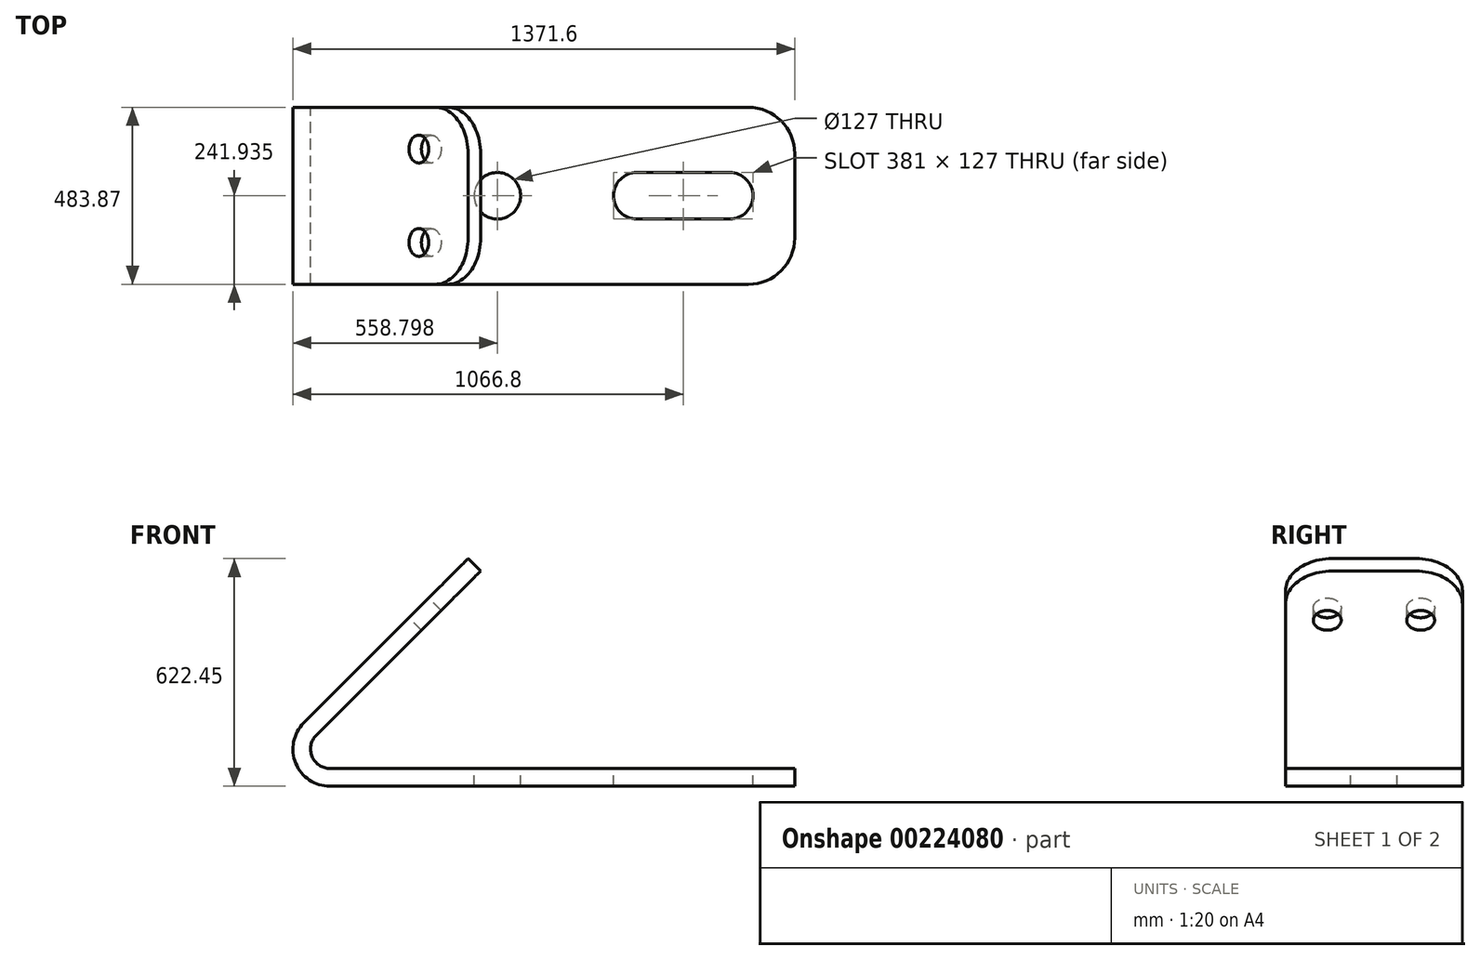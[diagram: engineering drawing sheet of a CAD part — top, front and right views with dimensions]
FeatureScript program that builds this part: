
annotation { "Feature Type Name" : "Feature", "Feature Type Description" : "" }
export const myFeature = defineFeature(function(context is Context, id is Id, definition is map)
    precondition{}
    {
        {
            var Q0;
            Q0=qCreatedBy(makeId("Front.planeOp"),FACE);
            var sketch = newSketch(context, id + "F0", { "sketchPlane" : qUnion([Q0])});
            skLineSegment(sketch, "E0", {"start": v(713.7, 0) * mm, "end": v(-556.3, 0) * mm});
            skLineSegment(sketch, "E1", {"start": v(-628.14, 173.44) * mm, "end": v(-179.13, 622.45) * mm});
            skPoint(sketch, "E2.visualSharp", {"position": v(-801.59, 0) * mm});
            skArc(sketch, "E2.filletArc", {"start": v(-628.14, 173.44) * mm, "mid": v(-650.17, 62.72) * mm, "end": v(-556.3, 0) * mm});
            skLineSegment(sketch, "E3", {"start": v(713.7, 0) * mm, "end": v(713.7, 48.26) * mm});
            skLineSegment(sketch, "E4", {"start": v(713.7, 48.26) * mm, "end": v(-556.3, 48.26) * mm});
            skLineSegment(sketch, "E5", {"start": v(-179.13, 622.45) * mm, "end": v(-145, 588.33) * mm});
            skLineSegment(sketch, "E6", {"start": v(-145, 588.33) * mm, "end": v(-594.02, 139.32) * mm});
            skPoint(sketch, "E7.newPointB", {"position": v(0, 48.26) * mm});
            skArc(sketch, "E7.filletArc", {"start": v(-594.02, 139.32) * mm, "mid": v(-605.58, 81.19) * mm, "end": v(-556.3, 48.26) * mm});
            skSolve(sketch);
        }
        {
            var Q0;
            Q0 = qSketchRegion(id + "F0", true);
            extrude(context, id + "F1", {"entities" : qUnion([Q0]), "depth" : 483.87 * mm});
        }
        {
            var Q0;
            Q0=makeQuery(id+"F1.opExtrude","SWEPT_FACE",FACE,{"disambiguationData":[OSD([sQuery(id+"F0.wireOp",EDGE,"E1")])]});
            var sketch = newSketch(context, id + "F2", { "sketchPlane" : qUnion([Q0])});
            skLineSegment(sketch, "E8", {"start": v(241.94, 313.48) * mm, "end": v(241.94, -745.94) * mm, "construction": true});
            skPoint(sketch, "E8.endSnap0", {"position": v(241.94, -321.52) * mm});
            skCircle(sketch, "E9", {"center": v(114.3, 122.98) * mm, "radius": 38.1 * mm});
            skCircle(sketch, "E10.MirrorC", {"center": v(369.57, 122.98) * mm, "radius": 38.1 * mm});
            skSolve(sketch);
        }
        {
            var Q0;
            Q0 = qSketchRegion(id + "F2", true);
            var Q1;
            Q1=makeQuery(id+"F1.opExtrude","SWEPT_FACE",FACE,{"disambiguationData":[OSD([sQuery(id+"F0.wireOp",EDGE,"E6")])]});
            extrude(context, id + "F3", {"entities" : qUnion([Q0]), "operationType" : NewBodyOperationType.REMOVE, "endBound" : BoundingType.UP_TO_SURFACE, "oppositeDirection" : true, "endBoundEntityFace" : qUnion([Q1]), "depth" : 25.4 * mm});
        }
        {
            var Q0;
            Q0=makeQuery(id+"F1.opExtrude","SWEPT_FACE",FACE,{"disambiguationData":[OSD([sQuery(id+"F0.wireOp",EDGE,"E4")])]});
            var sketch = newSketch(context, id + "F4", { "sketchPlane" : qUnion([Q0])});
            skLineSegment(sketch, "E11", {"start": v(742.94, -241.94) * mm, "end": v(713.7, -241.94) * mm, "construction": true});
            skPoint(sketch, "E11.endSnap0", {"position": v(-556.3, -241.94) * mm});
            skArc(sketch, "E12", {"start": v(535.9, -305.44) * mm, "mid": v(599.4, -241.94) * mm, "end": v(535.9, -178.44) * mm});
            skArc(sketch, "E13", {"start": v(281.9, -178.44) * mm, "mid": v(218.4, -241.94) * mm, "end": v(281.9, -305.44) * mm});
            skLineSegment(sketch, "E14", {"start": v(281.9, -178.44) * mm, "end": v(535.9, -178.44) * mm});
            skLineSegment(sketch, "E15", {"start": v(281.9, -305.44) * mm, "end": v(535.9, -305.44) * mm});
            skCircle(sketch, "E16", {"center": v(-99.1, -241.94) * mm, "radius": 63.5 * mm});
            skSolve(sketch);
        }
        {
            var Q0;
            Q0=makeQuery(id+"F4.imprint","IMPRINT",FACE,{"disambiguationData":[TD([[makeQuery(id+"F4.imprint","IMPRINT",EDGE,{"derivedFrom":sQuery(id+"F4.wireOp",EDGE,"E12")}),1.0]])]});
            var Q1;
            Q1=makeQuery(id+"F4.imprint","IMPRINT",FACE,{"disambiguationData":[TD([[makeQuery(id+"F4.imprint","IMPRINT",EDGE,{"derivedFrom":sQuery(id+"F4.wireOp",EDGE,"E16")}),1.0]])]});
            extrude(context, id + "F5", {"entities" : qUnion([Q0, Q1]), "operationType" : NewBodyOperationType.REMOVE, "endBound" : BoundingType.THROUGH_ALL, "oppositeDirection" : true, "depth" : 25.4 * mm});
        }
        {
            var Q0;
            Q0=makeQuery(id+"F1.opExtrude","CAP_EDGE",EDGE,{"disambiguationData":[OSD([sQuery(id+"F0.wireOp",EDGE,"E3")])],"isStart":false});
            var Q1;
            Q1=makeQuery(id+"F1.opExtrude","CAP_EDGE",EDGE,{"disambiguationData":[OSD([sQuery(id+"F0.wireOp",EDGE,"E3")])],"isStart":true});
            var Q2;
            Q2=makeQuery(id+"F1.opExtrude","CAP_EDGE",EDGE,{"disambiguationData":[OSD([sQuery(id+"F0.wireOp",EDGE,"E5")])],"isStart":true});
            var Q3;
            Q3=makeQuery(id+"F1.opExtrude","CAP_EDGE",EDGE,{"disambiguationData":[OSD([sQuery(id+"F0.wireOp",EDGE,"E5")])],"isStart":false});
            fillet(context, id + "F6", {"entities" : qUnion([Q0, Q1, Q2, Q3]), "radius" : 127 * mm, "tangentPropagation" : true, "allowEdgeOverflow" : false});
        }
    });
